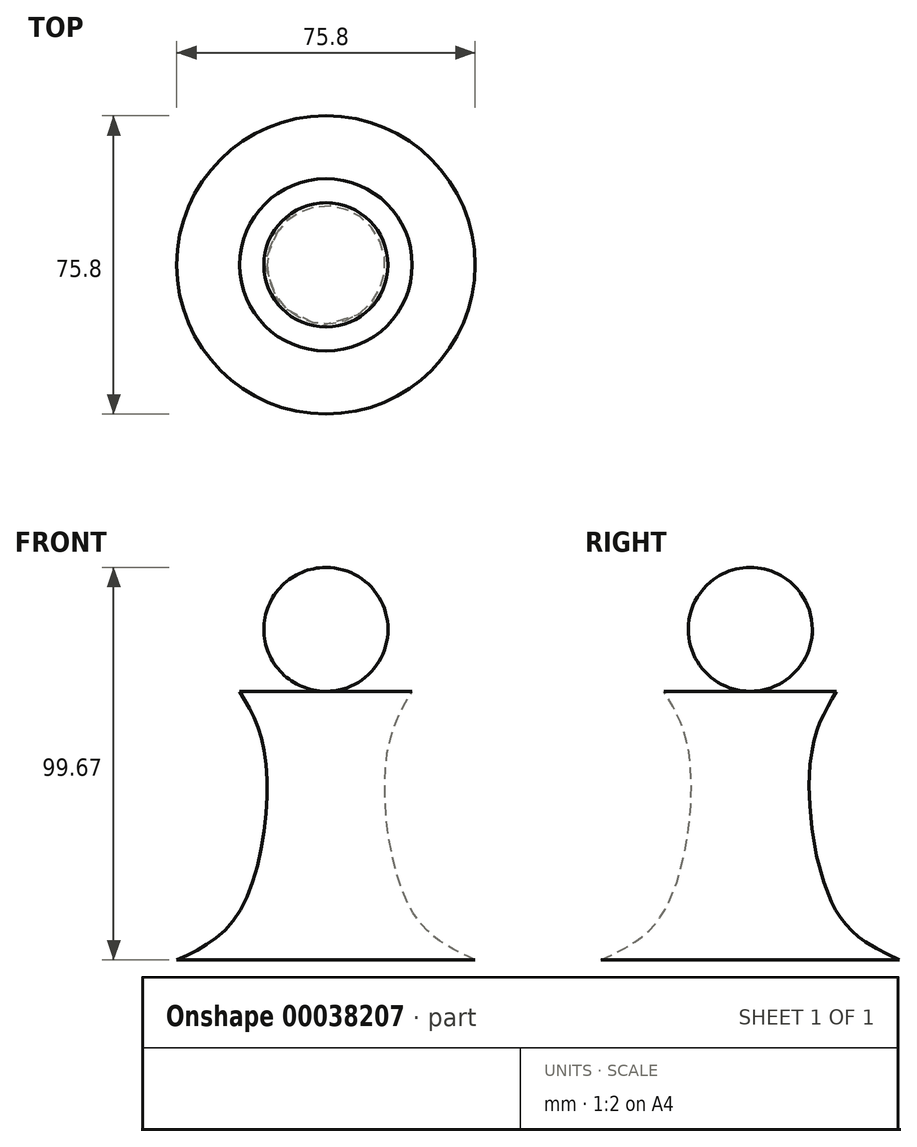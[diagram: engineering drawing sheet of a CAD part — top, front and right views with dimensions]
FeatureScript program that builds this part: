
annotation { "Feature Type Name" : "Feature", "Feature Type Description" : "" }
export const myFeature = defineFeature(function(context is Context, id is Id, definition is map)
    precondition{}
    {
        {
            var Q0;
            Q0=qCreatedBy(makeId("Front.planeOp"),FACE);
            var sketch = newSketch(context, id + "F0", { "sketchPlane" : qUnion([Q0])});
            skArc(sketch, "E0", {"start": v(0, 19.51) * mm, "mid": v(15.77, 35.23) * mm, "end": v(0, 50.96) * mm});
            skLineSegment(sketch, "E1", {"start": v(0, 19.51) * mm, "end": v(21.9, 19.45) * mm});
            skFitSpline(sketch, "E2", {"points": [v(21.9, 19.45) * mm, v(15.44, 2.95) * mm, v(21.9, -36.36) * mm, v(37.9, -48.7) * mm], "startDerivative": vector(-29.02, -47.93) * mm, "endDerivative": vector(59.5, -26.98) * mm});
            skLineSegment(sketch, "E3", {"start": v(37.9, -48.7) * mm, "end": v(0, -48.7) * mm});
            skLineSegment(sketch, "E4", {"start": v(0, -48.7) * mm, "end": v(0, 50.96) * mm});
            skSolve(sketch);
        }
        {
            var Q0;
            Q0 = qSketchRegion(id + "F0", true);
            var Q1;
            Q1=sQuery(id+"F0.wireOp",EDGE,"E4");
            revolve(context, id + "F1", {"entities" : qUnion([Q0]), "axis" : qUnion([Q1]), "revolveType" : RevolveType.FULL});
        }
    });
